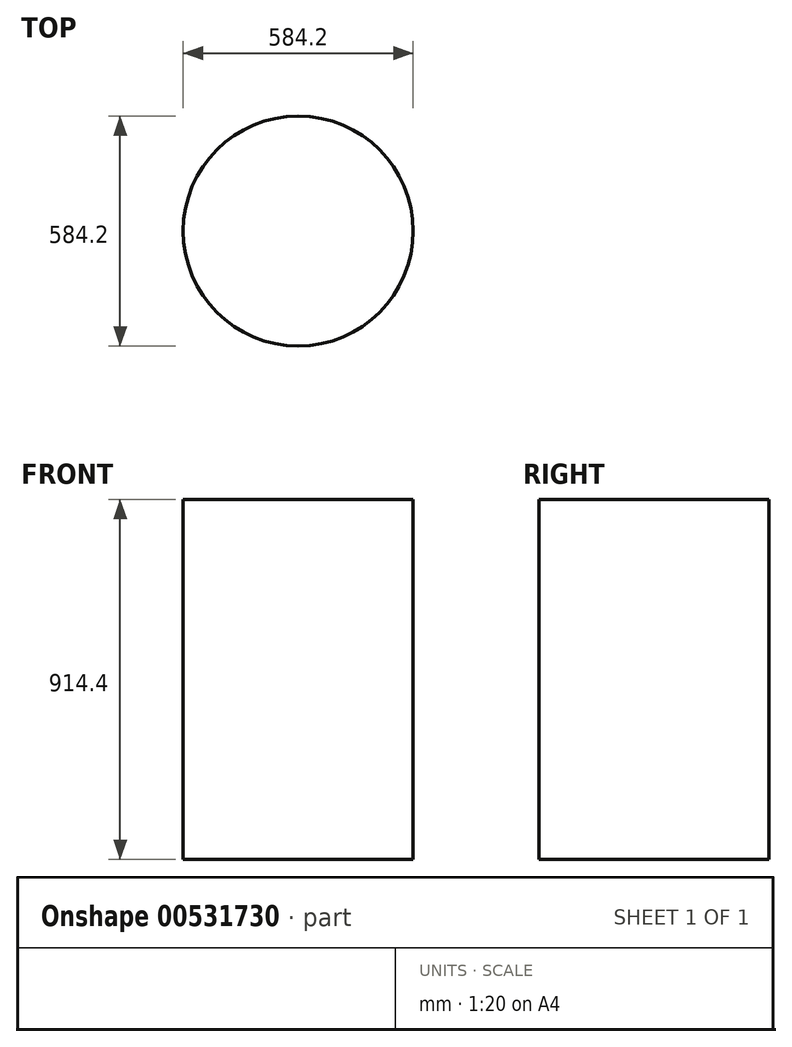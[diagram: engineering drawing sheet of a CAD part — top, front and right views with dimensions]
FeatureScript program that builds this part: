
annotation { "Feature Type Name" : "Feature", "Feature Type Description" : "" }
export const myFeature = defineFeature(function(context is Context, id is Id, definition is map)
    precondition{}
    {
        {
            var Q0;
            Q0=qCreatedBy(makeId("Top.planeOp"),FACE);
            var sketch = newSketch(context, id + "F0", { "sketchPlane" : qUnion([Q0])});
            skCircle(sketch, "E0", {"center": v(0, 0) * mm, "radius": 292.1 * mm});
            skSolve(sketch);
        }
        {
            var Q0;
            Q0=makeQuery(id+"F0.imprint","IMPRINT",FACE,{"disambiguationData":[TD([[makeQuery(id+"F0.imprint","IMPRINT",EDGE,{"derivedFrom":sQuery(id+"F0.wireOp",EDGE,"E0")}),1.0]])]});
            extrude(context, id + "F1", {"entities" : qUnion([Q0]), "depth" : 914.4 * mm, "offsetDistance" : 25.4 * mm});
        }
    });
